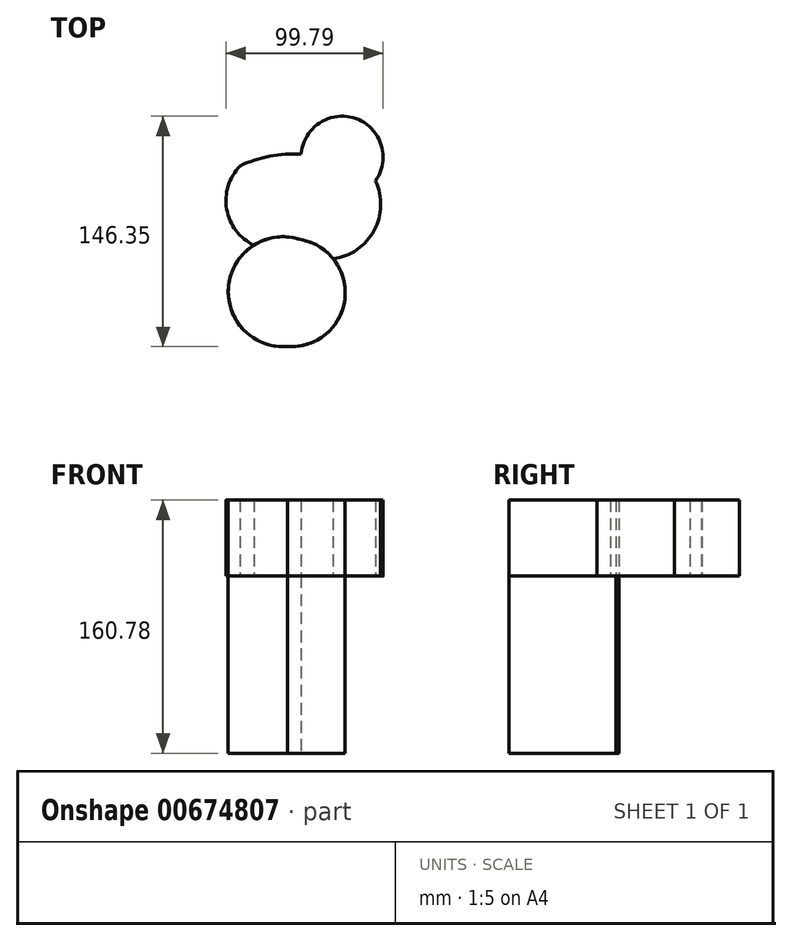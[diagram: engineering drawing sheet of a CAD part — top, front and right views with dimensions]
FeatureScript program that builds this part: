
annotation { "Feature Type Name" : "Feature", "Feature Type Description" : "" }
export const myFeature = defineFeature(function(context is Context, id is Id, definition is map)
    precondition{}
    {
        {
            var Q0;
            Q0=qCreatedBy(makeId("Top.planeOp"),FACE);
            var sketch = newSketch(context, id + "F0", { "sketchPlane" : qUnion([Q0])});
            skArc(sketch, "E0", {"start": v(-186.52, 13.56) * mm, "mid": v(-150.24, 43.4) * mm, "end": v(-177.94, 81.32) * mm});
            skArc(sketch, "E1", {"start": v(-177.94, 81.32) * mm, "mid": v(-223.99, 52.73) * mm, "end": v(-186.52, 13.56) * mm});
            skSolve(sketch);
        }
        {
            var Q0;
            Q0=makeQuery(id+"F0.imprint","IMPRINT",FACE,{"disambiguationData":[TD([[makeQuery(id+"F0.imprint","IMPRINT",EDGE,{"derivedFrom":sQuery(id+"F0.wireOp",EDGE,"E0")}),1.0]])]});
            extrude(context, id + "F1", {"entities" : qUnion([Q0]), "depth" : 112.52 * mm, "offsetDistance" : 25.4 * mm});
        }
        {
            var Q0;
            Q0=makeQuery(id+"F1.opExtrude","CAP_FACE",FACE,{"disambiguationData":[OSD([sQuery(id+"F0.wireOp",EDGE,"E0"),sQuery(id+"F0.wireOp",EDGE,"E1")])],"isStart":false});
            var sketch = newSketch(context, id + "F2", { "sketchPlane" : qUnion([Q0])});
            skArc(sketch, "E2", {"start": v(-216.86, 128.23) * mm, "mid": v(-225.24, 100.79) * mm, "end": v(-208, 77.85) * mm});
            skArc(sketch, "E3", {"start": v(-177.94, 135.64) * mm, "mid": v(-197.87, 134.4) * mm, "end": v(-216.86, 128.23) * mm});
            skArc(sketch, "E4", {"start": v(-130.76, 118.64) * mm, "mid": v(-143.14, 158.24) * mm, "end": v(-177.94, 135.64) * mm});
            skArc(sketch, "E5", {"start": v(-157.62, 69.25) * mm, "mid": v(-131.64, 87.12) * mm, "end": v(-130.76, 118.64) * mm});
            skSolve(sketch);
        }
        {
            var Q0;
            Q0 = qSketchRegion(id + "F2", true);
            var Q1;
            {var subQ1=sQuery(id+"F2.wireOp",EDGE,"E2");Q1=makeQuery(id+"F2.imprint","IMPRINT",FACE,{"disambiguationData":[TD([[makeQuery(id+"F2.imprint","IMPRINT",EDGE,{"derivedFrom":subQ1}),1.0]])]});}
            extrude(context, id + "F3", {"entities" : qUnion([Q0, Q1]), "depth" : 48.26 * mm, "offsetDistance" : 25.4 * mm});
        }
        {
            var Q0;
            Q0=makeQuery(id+"F1.opExtrude","CAP_FACE",FACE,{"disambiguationData":[OSD([sQuery(id+"F0.wireOp",EDGE,"E0"),sQuery(id+"F0.wireOp",EDGE,"E1")])],"isStart":false});
            extrude(context, id + "F4", {"entities" : qUnion([Q0]), "depth" : 48.26 * mm, "offsetDistance" : 25.4 * mm});
        }
    });
